# Revit family: Pump_Commercial-Effluent-Zoeller-130_Automatic_Series
name_source: partatom
category: Mechanical Equipment
revit_build: Autodesk Revit 2014 (Build: 20130308_1515(x64)
units: mm (PartAtom-declared; Revit-internal decimal feet)

## types (8) — shared parameters
Assembly Code = D2010900
Cooling = Oil Filled
Cord Length = 120"
Cord Type = UL Listed, neoprene
Default Elevation = 0"
Description = Automatic Cast Iron Commercial Effluent or dewatering submersible pump for septic tank, low pressure pipe (LPP) and enhanced flow STEP systems.
Discharge Diameter = 1 1/2" NPT
Discharge Height = 3 15/16"
Discharge Radius = 3/4"
Height = 12 3/4"
Hertz = 60
Installation Type = Floor Mounted
Insulation = Class A or B
Length = 12 1/4"
Manufacturer = Zoeller
Max Flow @ 5' = 90 GPM
Max. Water Temp. = 130 °F
Maximum Head = 312"
Motor = 1/2 HP
Motor Design Letter = NEMA B
Motor Thermal Shutoff = Auto Reset Thermal Overload.
Motor Type = Submersible
O-Rings and Cover Gasket = Neoprene
Off Point = 2 3/4"
On Point = 10"
Operation = Automatic
Phase = 1
Price = Prices may vary. Please consult Manufacturer Representative for most up-to-date price list.
Product Page URL = http://www.zoellerpumps.com
RPM = 1750
Shaft Seal = Carbon and Ceramic
Solid Handling = 5/8" Spherical Solids
Type = Split Phase
URL = http://www.zoellerpumps.com
Warranty Information = 36 Months (Limited)
Waste Connection = Yes
Width = 9 5/8"

## per-type parameters (varying)
| type | Amps | Apparent Load | Body Material | Impeller Type | Material | Model | Voltage |
| 137 - 115V 1Ph | 11 A | 1231 VA | Cast Iron-Zoeller-Powder Coated Epoxy | Non-clogging vortex | Cast Iron-Zoeller-Powder Coated Epoxy | 137 | 115 V |
| 139 - 115V 1Ph | 11 A | 1231 VA | Metal-Zoeller-Bronze | Bronze Non-clogging vortex | Metal-Zoeller-Bronze | 139 | 115 V |
| 137 - 200V 1Ph | 6 A | 1240 VA | Cast Iron-Zoeller-Powder Coated Epoxy | Non-clogging vortex | Cast Iron-Zoeller-Powder Coated Epoxy | 137 | 200 V |
| 137 - 208V 1Ph | 11 A | 2226 VA | Cast Iron-Zoeller-Powder Coated Epoxy | Non-clogging vortex | Cast Iron-Zoeller-Powder Coated Epoxy | 137 | 208 V |
| 137 - 230V 1Ph | 6 A | 1334 VA | Cast Iron-Zoeller-Powder Coated Epoxy | Non-clogging vortex | Cast Iron-Zoeller-Powder Coated Epoxy | 137 | 230 V |
| 139 - 200V 1Ph | 3 A | 520 VA | Metal-Zoeller-Bronze | Bronze Non-clogging vortex | Metal-Zoeller-Bronze | 139 | 200 V |
| 139 - 208V 1Ph | 11 A | 2226 VA | Metal-Zoeller-Bronze | Bronze Non-clogging vortex | Metal-Zoeller-Bronze | 139 | 208 V |
| 139 - 230V 1Ph | 3 A | 598 VA | Metal-Zoeller-Bronze | Bronze Non-clogging vortex | Metal-Zoeller-Bronze | 139 | 230 V |

## geometry (parser evidence)
native form markers: Sweep x1
no freeform markers — native parametric forms only
